# Revit family: LS22 Square Coffee Table
name_source: partatom
category: Furniture
revit_build: Autodesk Revit 2016 (Build: 20160525_1230(x64)
units: mm (PartAtom-declared; Revit-internal decimal feet)

## family parameters
Always vertical = Yes
Cut with Voids When Loaded = No
OmniClass Number = 23.40.20.00
OmniClass Title = General Furniture and Specialties
Room Calculation Point = No
Shared = No
Work Plane-Based = No

## types (3) — shared parameters
Frame = Gresham - Silver Metal
Manufacturer = Gresham Office Furniture
Range = LS23
Table Top = Gresham - Walnut
URL = www.gof.co.uk

## per-type parameters (varying)
| type | 700 Frame | 800 Frame | 900 Frame | Product Code | Width |
| 600 x 600 | Yes | No | No | LS23B1 | 600 mm |
| 700 x 700 | No | Yes | No | LS23B2 | 700 mm  [stored 2.29659 ft] |
| 800 x 800 | No | No | Yes | LS23B3 | 800 mm  [stored 2.62467 ft] |

note: [stored X ft] marks values corroborated as IEEE doubles in the binary element streams (Revit-internal decimal feet)

## geometry (parser evidence)
native form markers: Blend x8, Sweep x10
no freeform markers — native parametric forms only
